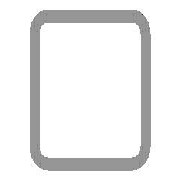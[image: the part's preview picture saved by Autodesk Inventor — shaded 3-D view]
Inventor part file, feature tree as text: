
AUTODESK INVENTOR PART (.ipt)
format: ipt  version: 2025 (Build 290162010, 162A)  size: 135,680 bytes
history: native  units: mm (DEFAULTED — no unit token found)
features: other x4, sketch x1, plane x1
ambient origin geometry x8: Origin, YZ Plane, XZ Plane, XY Plane, X Axis, Y Axis, Z Axis, Center Point
bodies: Solid1 (feature_tree), Body (feature_tree)
feature tree (6):
  parser-record x1  (decoder bookkeeping rows leaked as tree rows — omitted from the tree; the rows remain in map.json)
  other  "Driven Length"
  other  "Start Plane"
  other  "End Plane"
  sketch  "Sketch3"  dims[d3=1900.0mm d4=0.0mm d7=4.0mm d9=40.0mm d11=40.0mm d12=2.0mm d13=-0.0mm d14=1900.0mm d15=20.0mm d16=20.0mm d17=90.0deg d18=1900.0mm]
  plane  "Work Plane3"
